FCSTD DOCUMENT  (FreeCAD 0.19R18353 (Git))
Label: base_dimensions
License: CreativeCommons Attribution-ShareAlike
LicenseURL: http://creativecommons.org/licenses/by-sa/4.0/
objects: Sketcher::SketchObject×10, PartDesign::Body×3, App::Link×2, App::Part×2, Spreadsheet::Sheet×1
note: 13 computed .brp shape members not serialized (recipe doc carries the construction recipe); baked Part::Feature solids carry a one-line shape summary decoded from their .brp

FEATURE [Sketcher::SketchObject] Sketch  label="front_outline_sketch"
  MapMode = 5
  Placement = pos=(0,0,0) rot=(1,0,0;1.5708rad)
  Support = -> [XZ_Plane001]
  expr: .Constraints.height = .Constraints.side_height + 30mm
  sketch-geometry (8):
    g0: LineSegment [constr] StartX=-80 StartY=120 StartZ=0 EndX=80 EndY=120 EndZ=0
    g1: LineSegment StartX=80 StartY=120 StartZ=0 EndX=80 EndY=0 EndZ=0
    g2: LineSegment StartX=80 StartY=0 StartZ=0 EndX=-80 EndY=0 EndZ=0
    g3: LineSegment StartX=-80 StartY=0 StartZ=0 EndX=-80 EndY=120 EndZ=0
    g4: ArcOfCircle CenterX=-3e-14 CenterY=-13.3333 CenterZ=0 NormalX=0 NormalY=0 NormalZ=1 AngleXU=0 Radius=163.333 StartAngle=1.1172 EndAngle=2.02439
    g5: LineSegment [constr] StartX=0 StartY=150 StartZ=0 EndX=0 EndY=0 EndZ=0
    g6: ArcOfCircle CenterX=-65 CenterY=120 CenterZ=0 NormalX=0 NormalY=0 NormalZ=1 AngleXU=0 Radius=15 StartAngle=2.02439 EndAngle=3.14159
    g7: ArcOfCircle CenterX=65 CenterY=120 CenterZ=0 NormalX=0 NormalY=0 NormalZ=1 AngleXU=0 Radius=15 StartAngle=9e-16 EndAngle=1.1172
  constraints (20):
    c: Coincident(g0,g1)
    c: Coincident(g1,g2)
    c: Coincident(g2,g3)
    c: Coincident(g3,g0)
    c: Horizontal(g0)
    c: Horizontal(g2)
    c: Vertical(g3)
    c: Symmetric(g2,g2,g-1)
    c: DistanceX(g2,g2) = 160
    c: DistanceY(g3,g3) = 120  'side_height'
    c: Coincident(g5,g-1)
    c: Perpendicular(g5,g4) = 4.71239
    c: Equal(g7,g6)
    c: Radius(g6) = 15
    c: Tangent(g6,g3) = 1.5708
    c: Tangent(g6,g4) = -1.5708
    c: Tangent(g7,g4) = -1.5708
    c: DistanceY(g5,g5) = 150  'height'
    c: PointOnObject(g5,g-2)
    c: Tangent(g7,g1) = 1.5708
FEATURE [Sketcher::SketchObject] Sketch001  label="front_y"
  MapMode = 5
  Support = -> [XY_Plane001]
  sketch-geometry (3):
    g0: LineSegment StartX=0 StartY=-5 StartZ=0 EndX=0 EndY=0 EndZ=0
    g1: LineSegment StartX=0 StartY=0 StartZ=0 EndX=0 EndY=10 EndZ=0
    g2: LineSegment StartX=0 StartY=10 StartZ=0 EndX=0 EndY=110 EndZ=0
  constraints (9):
    c: Coincident(g0,g1)
    c: Coincident(g1,g2)
    c: Vertical(g2)
    c: DistanceY(g0,g0) = 5  'deco_thickness'
    c: Coincident(g0,g-1)
    c: Vertical(g0)
    c: Vertical(g1)
    c: DistanceY(g1,g1) = 10  'thickness'
    c: DistanceY(g2) = 110  'case_depth'
FEATURE [Sketcher::SketchObject] Sketch002  label="box_cutout_sketch"
  MapMode = 5
  Placement = pos=(0,0,0) rot=(1,0,0;1.5708rad)
  Support = -> [XZ_Plane003]
  sketch-geometry (7):
    g0: LineSegment StartX=-15 StartY=9e-16 StartZ=0 EndX=-7.5 EndY=-12.9904 EndZ=0
    g1: LineSegment StartX=-7.5 StartY=-12.9904 StartZ=0 EndX=7.5 EndY=-12.9904 EndZ=0
    g2: LineSegment StartX=7.5 StartY=-12.9904 StartZ=0 EndX=15 EndY=1.8e-15 EndZ=0
    g3: LineSegment StartX=15 StartY=1.8e-15 StartZ=0 EndX=7.5 EndY=12.9904 EndZ=0
    g4: LineSegment StartX=7.5 StartY=12.9904 StartZ=0 EndX=-7.5 EndY=12.9904 EndZ=0
    g5: LineSegment StartX=-7.5 StartY=12.9904 StartZ=0 EndX=-15 EndY=1.8e-15 EndZ=0
    g6: Circle [constr] CenterX=0 CenterY=0 CenterZ=0 NormalX=0 NormalY=0 NormalZ=1 AngleXU=0 Radius=15
  constraints (16):
    c: Coincident(g0,g1)
    c: Coincident(g1,g2)
    c: Coincident(g2,g3)
    c: Coincident(g3,g4)
    c: Coincident(g4,g5)
    c: Coincident(g5,g0)
    c: Equal(g0, g1-g5) x5
    c: PointOnObject(g0,g6)
    c: PointOnObject(g1,g6)
    c: PointOnObject(g2,g6)
    c: PointOnObject(g3,g6)
    c: PointOnObject(g4,g6)
    c: PointOnObject(g5,g6)
    c: Horizontal(g1)
    c: DistanceX(g0,g2) = 30  'width'
    c: Coincident(g6,g-1)
FEATURE [Sketcher::SketchObject] Sketch003  label="box_outline_sketch"
  MapMode = 5
  Placement = pos=(0,0,0) rot=(1,0,0;1.5708rad)
  Support = -> [XZ_Plane003]
  sketch-geometry (8):
    g0: LineSegment [constr] StartX=-15 StartY=-3.6e-15 StartZ=0 EndX=-7.5 EndY=-12.9904 EndZ=0
    g1: LineSegment [constr] StartX=-7.5 StartY=-12.9904 StartZ=0 EndX=7.5 EndY=-12.9904 EndZ=0
    g2: LineSegment [constr] StartX=7.5 StartY=-12.9904 StartZ=0 EndX=15 EndY=-1.07e-14 EndZ=0
    g3: LineSegment [constr] StartX=15 StartY=-1.07e-14 StartZ=0 EndX=7.5 EndY=12.9904 EndZ=0
    g4: LineSegment [constr] StartX=7.5 StartY=12.9904 StartZ=0 EndX=-7.5 EndY=12.9904 EndZ=0
    g5: LineSegment [constr] StartX=-7.5 StartY=12.9904 StartZ=0 EndX=-15 EndY=-3.6e-15 EndZ=0
    g6: Circle [constr] CenterX=0 CenterY=0 CenterZ=0 NormalX=0 NormalY=0 NormalZ=1 AngleXU=0 Radius=15
    g7: Circle CenterX=0 CenterY=0 CenterZ=0 NormalX=0 NormalY=0 NormalZ=1 AngleXU=0 Radius=25
  constraints (18):
    c: Coincident(g0,g1)
    c: Coincident(g1,g2)
    c: Coincident(g2,g3)
    c: Coincident(g3,g4)
    c: Coincident(g4,g5)
    c: Coincident(g5,g0)
    c: Equal(g0, g1-g5) x5
    c: PointOnObject(g0,g6)
    c: PointOnObject(g1,g6)
    c: PointOnObject(g2,g6)
    c: PointOnObject(g3,g6)
    c: PointOnObject(g4,g6)
    c: PointOnObject(g5,g6)
    c: Horizontal(g1)
    c: DistanceX(g0,g2) = 30
    c: Coincident(g7,g6)
    c: Diameter(g7) = 50  'width'
    c: Coincident(g7,g-1)
FEATURE [Sketcher::SketchObject] Sketch004  label="box_positions"
  MapMode = 5
  Placement = pos=(0,0,0) rot=(1,0,0;1.5708rad)
  Support = -> [XZ_Plane001]
  sketch-geometry (2):
    g0: GeomPoint X=-40 Y=105 Z=0
    g1: GeomPoint X=30 Y=60 Z=0
  constraints (4):
    c: DistanceX(g0) = -40  'p1_x'
    c: DistanceY(g0) = 105  'p1_z'
    c: DistanceX(g1) = 30  'p2_x'
    c: DistanceY(g1) = 60  'p2_z'
FEATURE [PartDesign::Body] Body  label="base"
  Group = -> [Sketch,Sketch001,Sketch004]
  Origin = -> Origin001
FEATURE [PartDesign::Body] Body001  label="box"
  Group = -> [Sketch003,Sketch002]
  Origin = -> Origin003
FEATURE [App::Link] Link  label="box001"
  LinkPlacement = pos=(-40,0,105) rot=(0,0,1;0rad)
  LinkedObject = -> Body001
  Placement = pos=(-40,0,105) rot=(0,0,1;0rad)
  expr: .Placement.Base.x = <<base_dimensions>>#<<box_positions>>.Constraints.p1_x
  expr: .Placement.Base.y = 0
  expr: .Placement.Base.z = <<base_dimensions>>#<<box_positions>>.Constraints.p1_z
FEATURE [App::Link] Link001  label="box002"
  LinkPlacement = pos=(30,0,60) rot=(0,0,1;0rad)
  LinkedObject = -> Body001
  Placement = pos=(30,0,60) rot=(0,0,1;0rad)
  expr: .Placement.Base.x = <<base_dimensions>>#<<box_positions>>.Constraints.p2_x
  expr: .Placement.Base.y = 0
  expr: .Placement.Base.z = <<base_dimensions>>#<<box_positions>>.Constraints.p2_z
FEATURE [App::Part] Part001  label="preview"
  Group = -> [Link,Link001]
  Origin = -> Origin002
FEATURE [Sketcher::SketchObject] Sketch005  label="lamp_base_sketch"
  MapMode = 5
  Placement = pos=(0,0,0) rot=(1,0,0;1.5708rad)
  Support = -> [XZ_Plane004]
  sketch-geometry (1):
    g0: Circle CenterX=0 CenterY=0 CenterZ=0 NormalX=0 NormalY=0 NormalZ=1 AngleXU=0 Radius=5
  constraints (2):
    c: Coincident(g0,g-1)
    c: Radius(g0) = 5  'radius'
FEATURE [Sketcher::SketchObject] Sketch006  label="lamp_outline_sketch"
  MapMode = 5
  Placement = pos=(0,0,0) rot=(1,0,0;1.5708rad)
  Support = -> [XZ_Plane004]
  expr: .Constraints.radius = <<lamp_base_sketch>>.Constraints.radius + <<data>>.lamp_fillet_radius + 0.5mm
  sketch-geometry (1):
    g0: Circle CenterX=0 CenterY=0 CenterZ=0 NormalX=0 NormalY=0 NormalZ=1 AngleXU=0 Radius=10.5
  constraints (2):
    c: Coincident(g0,g-1)
    c: Radius(g0) = 10.5  'radius'
FEATURE [Spreadsheet::Sheet] Spreadsheet  label="data"
  cells = A1=lamp fillet radius; B1(lamp_fillet_radius)==5mm
FEATURE [Sketcher::SketchObject] Sketch007  label="lamp_cutout_sketch"
  MapMode = 5
  Placement = pos=(0,0,0) rot=(1,0,0;1.5708rad)
  Support = -> [XZ_Plane004]
  expr: .Constraints.radius = <<lamp_base_sketch>>.Constraints.radius + 2mm
  sketch-geometry (1):
    g0: Circle CenterX=0 CenterY=0 CenterZ=0 NormalX=0 NormalY=0 NormalZ=1 AngleXU=0 Radius=7
  constraints (2):
    c: Coincident(g0,g-1)
    c: Radius(g0) = 7  'radius'
FEATURE [Sketcher::SketchObject] Sketch008  label="lamp_cutout_in_sketch"
  MapMode = 5
  Placement = pos=(0,0,0) rot=(1,0,0;1.5708rad)
  Support = -> [XZ_Plane004]
  expr: .Constraints.radius = <<lamp_base_sketch>>.Constraints.radius + 0.050000000000000003mm
  sketch-geometry (1):
    g0: Circle CenterX=0 CenterY=0 CenterZ=0 NormalX=0 NormalY=0 NormalZ=1 AngleXU=0 Radius=5.05
  constraints (2):
    c: Coincident(g0,g-1)
    c: Radius(g0) = 5.05  'radius'
FEATURE [Sketcher::SketchObject] Sketch009  label="lamp_positions_sketch"
  MapMode = 5
  Placement = pos=(0,0,0) rot=(1,0,0;1.5708rad)
  Support = -> [XZ_Plane004]
  sketch-geometry (7):
    g0: LineSegment StartX=-40 StartY=18 StartZ=0 EndX=-20.9474 EndY=29 EndZ=0
    g1: LineSegment StartX=-20.9474 StartY=29 StartZ=0 EndX=-20.9474 EndY=51 EndZ=0
    g2: LineSegment StartX=-20.9474 StartY=51 StartZ=0 EndX=-40 EndY=62 EndZ=0
    g3: LineSegment StartX=-40 StartY=62 StartZ=0 EndX=-59.0526 EndY=51 EndZ=0
    g4: LineSegment StartX=-59.0526 StartY=51 StartZ=0 EndX=-59.0526 EndY=29 EndZ=0
    g5: LineSegment StartX=-59.0526 StartY=29 StartZ=0 EndX=-40 EndY=18 EndZ=0
    g6: Circle [constr] CenterX=-40 CenterY=40 CenterZ=0 NormalX=0 NormalY=0 NormalZ=1 AngleXU=0 Radius=22
  constraints (17):
    c: Coincident(g0,g1)
    c: Coincident(g1,g2)
    c: Coincident(g2,g3)
    c: Coincident(g3,g4)
    c: Coincident(g4,g5)
    c: Coincident(g5,g0)
    c: Equal(g0, g1-g5) x5
    c: PointOnObject(g0,g6)
    c: PointOnObject(g1,g6)
    c: PointOnObject(g2,g6)
    c: PointOnObject(g3,g6)
    c: PointOnObject(g4,g6)
    c: PointOnObject(g5,g6)
    c: DistanceX(g6) = -40  'center_x'
    c: DistanceY(g6) = 40  'center_z'
    c: Vertical(g1)
    c: Radius(g6) = 22  'radius'
FEATURE [PartDesign::Body] Body002  label="lamp"
  Group = -> [Sketch005,Sketch006,Sketch007,Sketch008,Sketch009]
  Origin = -> Origin004
FEATURE [App::Part] Part  label="dimensions"
  Group = -> [Body,Body001,Body002,Spreadsheet]
  Origin = -> Origin
